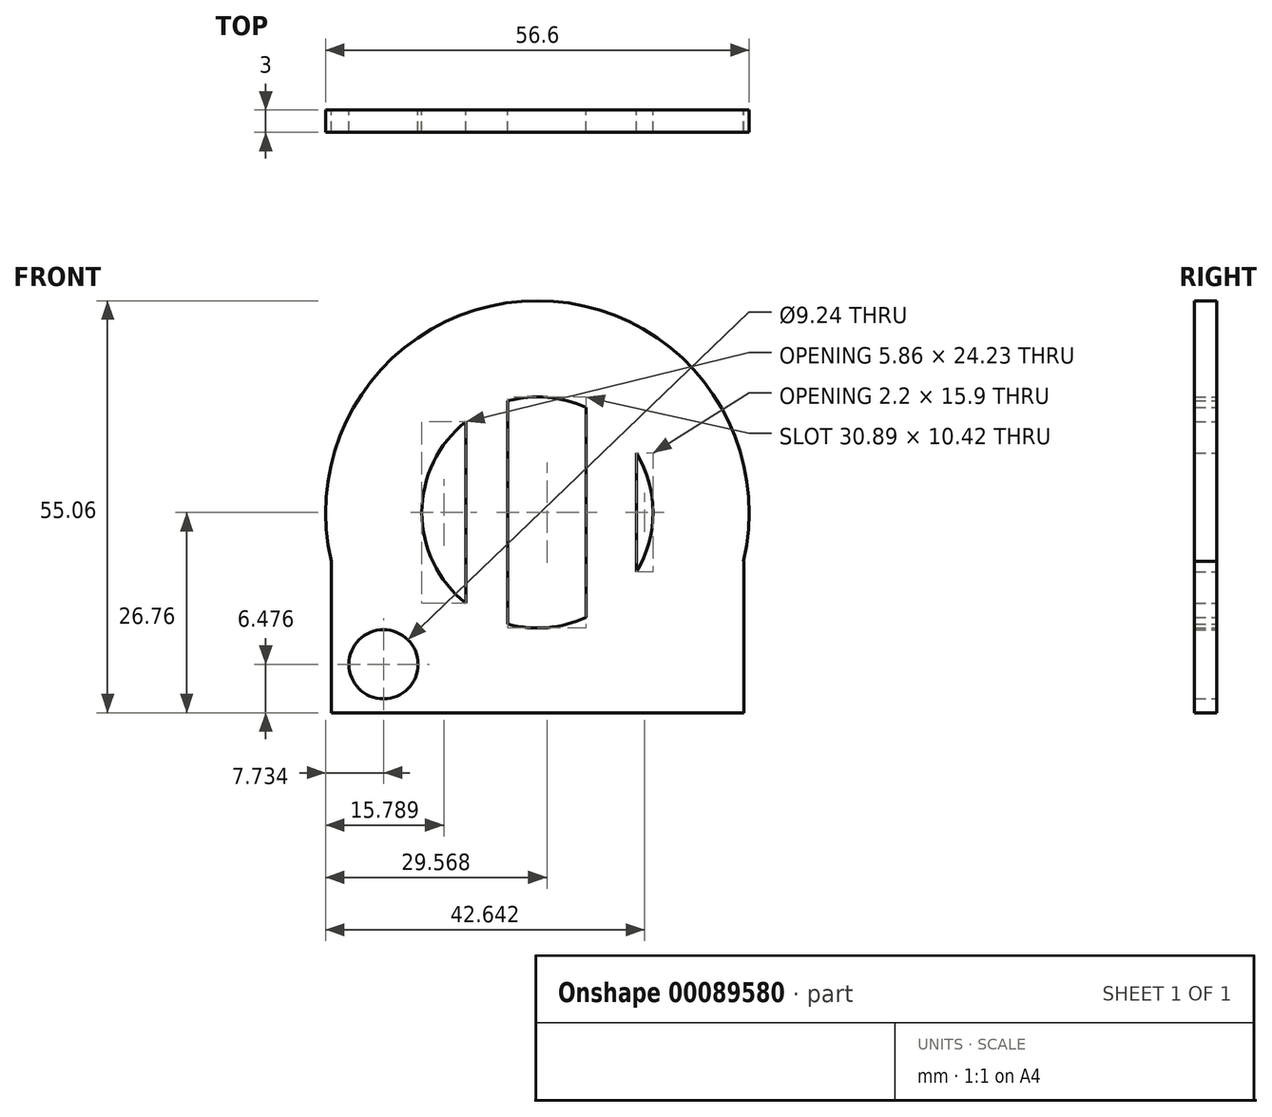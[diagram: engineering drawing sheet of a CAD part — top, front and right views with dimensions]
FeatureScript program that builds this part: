
annotation { "Feature Type Name" : "Feature", "Feature Type Description" : "" }
export const myFeature = defineFeature(function(context is Context, id is Id, definition is map)
    precondition{}
    {
        {
            var Q0;
            Q0=qCreatedBy(makeId("Front.planeOp"),FACE);
            var sketch = newSketch(context, id + "F0", { "sketchPlane" : qUnion([Q0])});
            skLineSegment(sketch, "E0.bottom", {"start": v(30, -30) * mm, "end": v(-30, -30) * mm, "construction": true});
            skLineSegment(sketch, "E0.top", {"start": v(30, 30) * mm, "end": v(-30, 30) * mm, "construction": true});
            skLineSegment(sketch, "E0.left", {"start": v(30, -30) * mm, "end": v(30, 30) * mm, "construction": true});
            skLineSegment(sketch, "E0.right", {"start": v(-30, -30) * mm, "end": v(-30, 30) * mm, "construction": true});
            skPoint(sketch, "E0.middle", {"position": v(0, 0) * mm});
            skLineSegment(sketch, "E1.bottom", {"start": v(27.6, -26.76) * mm, "end": v(-27.54, -26.76) * mm});
            skLineSegment(sketch, "E1.top", {"start": v(27.6, -6.5) * mm, "end": v(27.54, -6.5) * mm});
            skLineSegment(sketch, "E1.left", {"start": v(27.6, -26.76) * mm, "end": v(27.6, -6.5) * mm});
            skLineSegment(sketch, "E1.right", {"start": v(-27.54, -26.76) * mm, "end": v(-27.54, -6.5) * mm});
            skArc(sketch, "E2.trimOffspring", {"start": v(27.54, -6.5) * mm, "mid": v(0, 28.3) * mm, "end": v(-27.54, -6.5) * mm});
            skCircle(sketch, "E3", {"center": v(0, 0) * mm, "radius": 15.44 * mm});
            skLineSegment(sketch, "E4", {"start": v(-9.58, 12.11) * mm, "end": v(-9.58, -12.11) * mm});
            skLineSegment(sketch, "E5", {"start": v(-3.94, -14.93) * mm, "end": v(-3.94, 14.93) * mm});
            skLineSegment(sketch, "E6", {"start": v(6.48, -14.02) * mm, "end": v(6.48, 14.02) * mm});
            skLineSegment(sketch, "E7", {"start": v(13.24, -7.95) * mm, "end": v(13.24, 7.95) * mm});
            skPoint(sketch, "E8.orphan", {"position": v(-3.94, -18.6) * mm});
            skPoint(sketch, "E9.orphan", {"position": v(13.24, -18.6) * mm});
            skCircle(sketch, "E10", {"center": v(-20.57, -20.28) * mm, "radius": 4.62 * mm});
            skSolve(sketch);
        }
        {
            var Q0;
            Q0=makeQuery(id+"F0.imprint","IMPRINT",FACE,{"disambiguationData":[TD([[makeQuery(id+"F0.imprint","IMPRINT",EDGE,{"derivedFrom":sQuery(id+"F0.wireOp",EDGE,"E1.bottom")}),-1.0]])]});
            extrude(context, id + "F1", {"entities" : qUnion([Q0]), "depth" : 3 * mm});
        }
        {
            var Q0;
            {var subQ0=sQuery(id+"F0.wireOp",EDGE,"E4");Q0=makeQuery(id+"F0.imprint","IMPRINT",FACE,{"disambiguationData":[TD([[makeQuery(id+"F0.imprint","IMPRINT",EDGE,{"derivedFrom":subQ0}),1.0]])]});}
            var Q1;
            {var subQ0=sQuery(id+"F0.wireOp",EDGE,"E6");Q1=makeQuery(id+"F0.imprint","IMPRINT",FACE,{"disambiguationData":[TD([[makeQuery(id+"F0.imprint","IMPRINT",EDGE,{"derivedFrom":subQ0}),-1.0]])]});}
            extrude(context, id + "F2", {"entities" : qUnion([Q0, Q1]), "operationType" : NewBodyOperationType.ADD, "depth" : 3 * mm});
        }
    });
